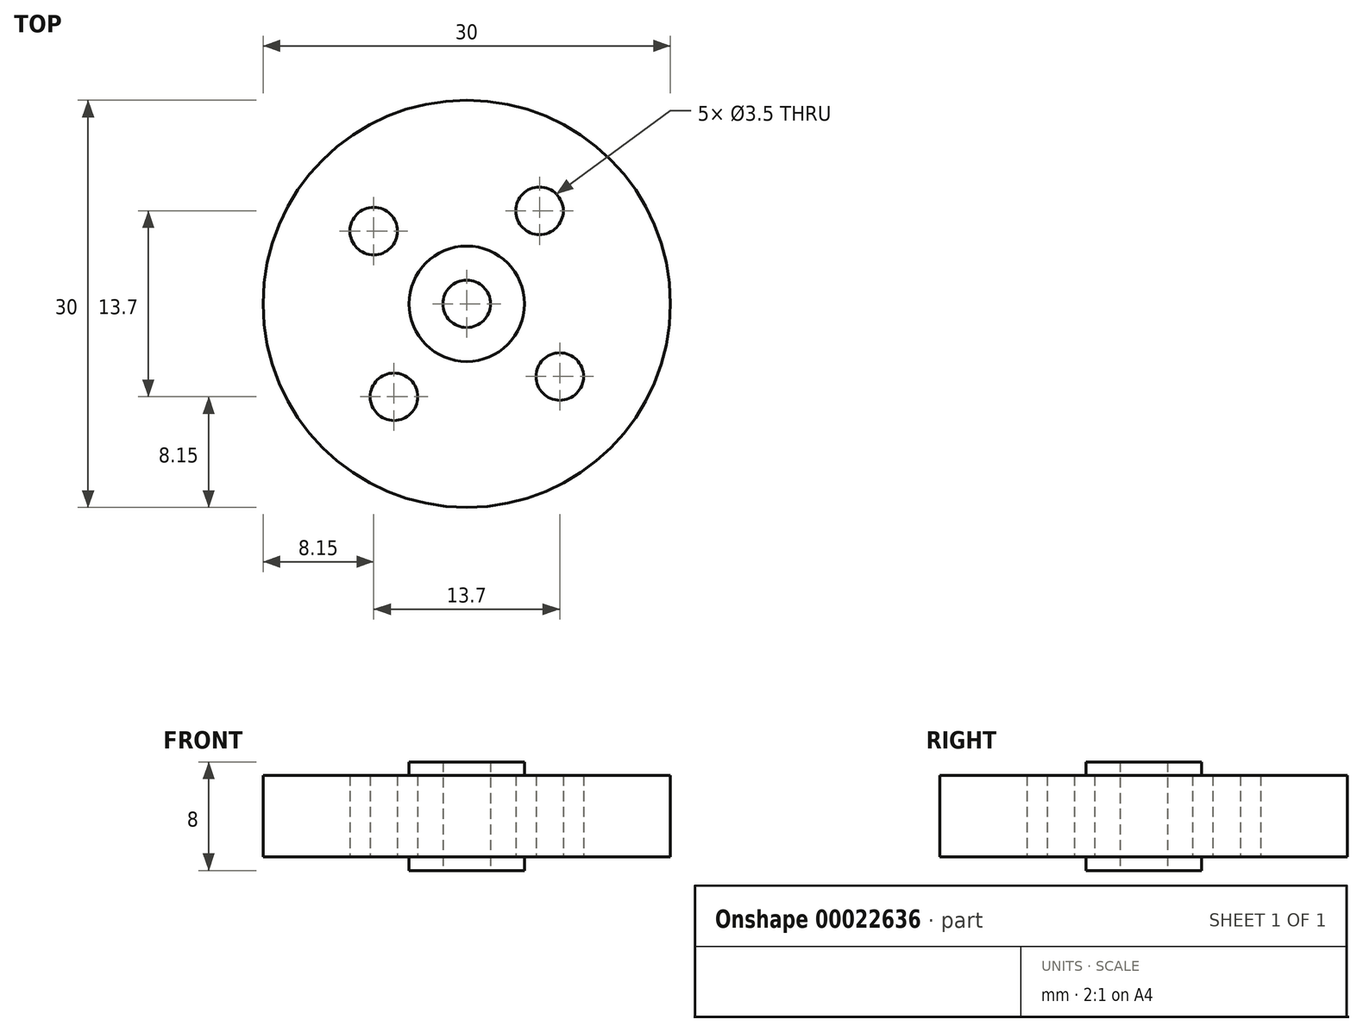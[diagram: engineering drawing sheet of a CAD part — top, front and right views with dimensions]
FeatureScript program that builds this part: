
annotation { "Feature Type Name" : "Feature", "Feature Type Description" : "" }
export const myFeature = defineFeature(function(context is Context, id is Id, definition is map)
    precondition{}
    {
        {
            var Q0;
            Q0=qCreatedBy(makeId("Top.planeOp"),FACE);
            var sketch = newSketch(context, id + "F0", { "sketchPlane" : qUnion([Q0])});
            skCircle(sketch, "E0", {"center": v(0, 0) * mm, "radius": 15 * mm});
            skCircle(sketch, "E1", {"center": v(-6.85, 5.36) * mm, "radius": 1.75 * mm});
            skCircle(sketch, "E2.1.0", {"center": v(-5.36, -6.85) * mm, "radius": 1.75 * mm});
            skCircle(sketch, "E2.2.0", {"center": v(6.85, -5.36) * mm, "radius": 1.75 * mm});
            skCircle(sketch, "E2.3.0", {"center": v(5.36, 6.85) * mm, "radius": 1.75 * mm});
            skCircle(sketch, "E3", {"center": v(0, 0) * mm, "radius": 1.75 * mm});
            skCircle(sketch, "E4", {"center": v(0, 0) * mm, "radius": 4.25 * mm});
            skSolve(sketch);
        }
        {
            var Q0;
            Q0=makeQuery(id+"F0.imprint","IMPRINT",FACE,{"disambiguationData":[TD([[makeQuery(id+"F0.imprint","IMPRINT",EDGE,{"derivedFrom":sQuery(id+"F0.wireOp",EDGE,"E0")}),1.0]])]});
            extrude(context, id + "F1", {"entities" : qUnion([Q0]), "endBound" : BoundingType.SYMMETRIC, "depth" : 6 * mm});
        }
        {
            var Q0;
            Q0=makeQuery(id+"F0.imprint","IMPRINT",FACE,{"disambiguationData":[TD([[makeQuery(id+"F0.imprint","IMPRINT",EDGE,{"derivedFrom":sQuery(id+"F0.wireOp",EDGE,"E3")}),-1.0]])]});
            extrude(context, id + "F2", {"entities" : qUnion([Q0]), "operationType" : NewBodyOperationType.ADD, "endBound" : BoundingType.SYMMETRIC, "depth" : 8 * mm});
        }
    });
